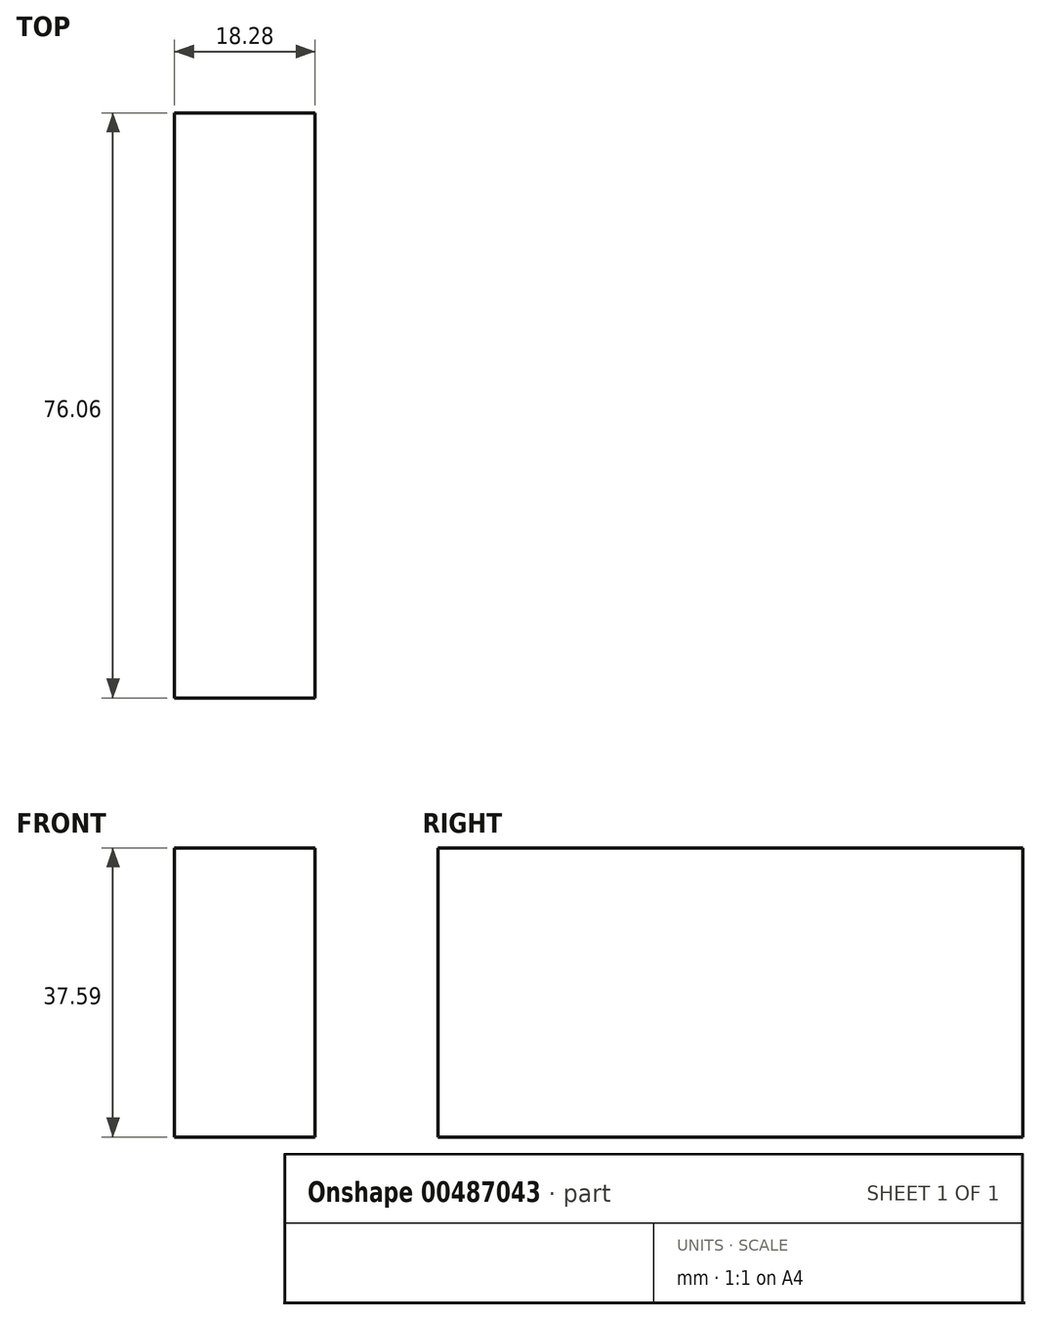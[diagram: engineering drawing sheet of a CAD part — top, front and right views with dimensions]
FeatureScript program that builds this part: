
annotation { "Feature Type Name" : "Feature", "Feature Type Description" : "" }
export const myFeature = defineFeature(function(context is Context, id is Id, definition is map)
    precondition{}
    {
        {
            var Q0;
            Q0=qCreatedBy(makeId("Top.planeOp"),FACE);
            var sketch = newSketch(context, id + "F0", { "sketchPlane" : qUnion([Q0])});
            skLineSegment(sketch, "E0.bottom", {"start": v(-56.45, 0) * mm, "end": v(-74.73, 0) * mm});
            skLineSegment(sketch, "E0.top", {"start": v(-56.45, 76.06) * mm, "end": v(-74.73, 76.06) * mm});
            skLineSegment(sketch, "E0.left", {"start": v(-56.45, 0) * mm, "end": v(-56.45, 76.06) * mm});
            skLineSegment(sketch, "E0.right", {"start": v(-74.73, 0) * mm, "end": v(-74.73, 76.06) * mm});
            skSolve(sketch);
        }
        {
            var Q0;
            Q0=makeQuery(id+"F0.imprint","IMPRINT",FACE,{"disambiguationData":[TD([[makeQuery(id+"F0.imprint","IMPRINT",EDGE,{"derivedFrom":sQuery(id+"F0.wireOp",EDGE,"E0.bottom")}),-1.0]])]});
            extrude(context, id + "F1", {"entities" : qUnion([Q0]), "depth" : 37.6 * mm, "offsetDistance" : 25.4 * mm});
        }
    });
